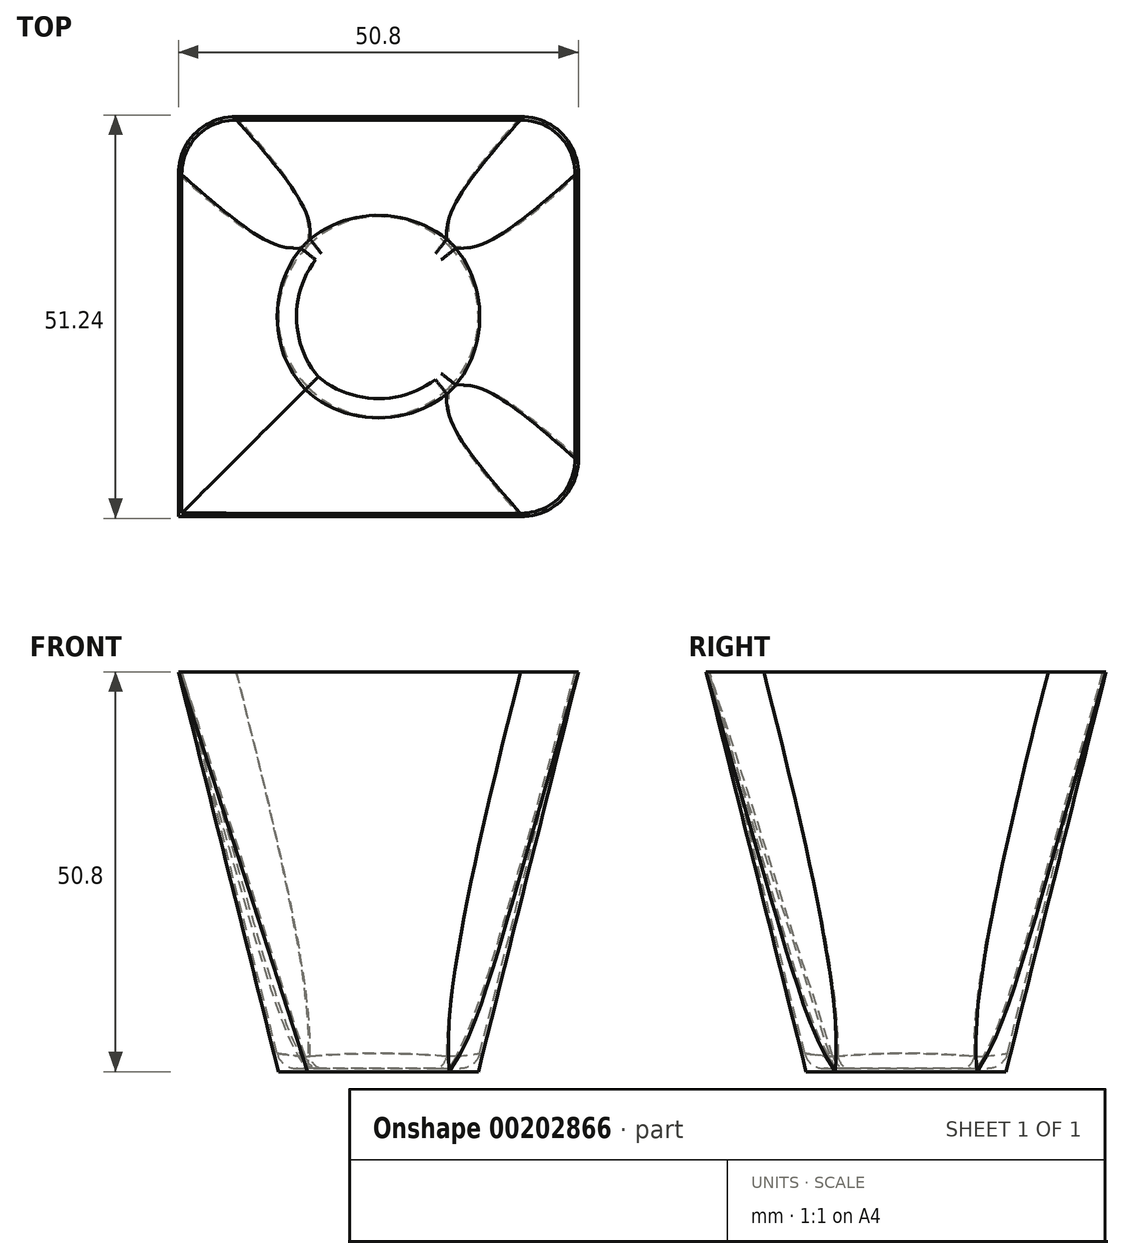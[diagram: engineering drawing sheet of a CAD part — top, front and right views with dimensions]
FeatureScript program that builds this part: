
annotation { "Feature Type Name" : "Feature", "Feature Type Description" : "" }
export const myFeature = defineFeature(function(context is Context, id is Id, definition is map)
    precondition{}
    {
        {
            var Q0;
            Q0=qCreatedBy(makeId("Top.planeOp"),FACE);
            var sketch = newSketch(context, id + "F0", { "sketchPlane" : qUnion([Q0])});
            skCircle(sketch, "E0", {"center": v(0, 0) * mm, "radius": 12.7 * mm});
            skSolve(sketch);
        }
        {
            var Q0;
            Q0=qCreatedBy(makeId("Top.planeOp"),FACE);
            cPlane(context, id + "F1", {"entities" : qUnion([Q0]), "cplaneType" : CPlaneType.OFFSET, "offset" : 50.8 * mm, "width" : 152.4 * mm, "height" : 152.4 * mm});
        }
        {
            var Q0;
            Q0=qCreatedBy(id+"F1.planeOp",FACE);
            var sketch = newSketch(context, id + "F2", { "sketchPlane" : qUnion([Q0])});
            skLineSegment(sketch, "E1.bottom", {"start": v(-25.4, 25.4) * mm, "end": v(25.4, 25.4) * mm});
            skLineSegment(sketch, "E1.top", {"start": v(-25.4, -25.4) * mm, "end": v(25.4, -25.4) * mm});
            skLineSegment(sketch, "E1.left", {"start": v(-25.4, 25.4) * mm, "end": v(-25.4, -25.4) * mm});
            skLineSegment(sketch, "E1.right", {"start": v(25.4, 25.4) * mm, "end": v(25.4, -25.4) * mm});
            skPoint(sketch, "E1.middle", {"position": v(0, 0) * mm});
            skSolve(sketch);
        }
        {
            var Q0;
            Q0=makeQuery(id+"F0.imprint","IMPRINT",FACE,{"disambiguationData":[TD([[makeQuery(id+"F0.imprint","IMPRINT",EDGE,{"derivedFrom":sQuery(id+"F0.wireOp",EDGE,"E0")}),1.0]])]});
            var Q1;
            Q1=makeQuery(id+"F2.imprint","IMPRINT",FACE,{"disambiguationData":[TD([[makeQuery(id+"F2.imprint","IMPRINT",EDGE,{"derivedFrom":sQuery(id+"F2.wireOp",EDGE,"E1.bottom")}),-1.0]])]});
            loft(context, id + "F3", {"sheetProfilesArray" : [{ "sheetProfileEntities" : qUnion([Q0]) }, { "sheetProfileEntities" : qUnion([Q1]) }]});
        }
        {
            var Q0;
            Q0=makeQuery(id+"F3.opLoft","SWEPT_EDGE",EDGE,{"disambiguationData":[OSD([sQuery(id+"F0.wireOp",EDGE,"E0"),sQuery(id+"F2.wireOp",EDGE,"E1.bottom"),sQuery(id+"F2.wireOp",EDGE,"E1.top"),sQuery(id+"F2.wireOp",EDGE,"E1.right")])]});
            var Q1;
            Q1=makeQuery(id+"F3.opLoft","SWEPT_EDGE",EDGE,{"disambiguationData":[OSD([sQuery(id+"F2.wireOp",EDGE,"E1.bottom"),sQuery(id+"F2.wireOp",EDGE,"E1.left")])]});
            var Q2;
            Q2=makeQuery(id+"F3.opLoft","SWEPT_EDGE",EDGE,{"disambiguationData":[OSD([sQuery(id+"F0.wireOp",EDGE,"E0"),sQuery(id+"F2.wireOp",EDGE,"E1.bottom"),sQuery(id+"F2.wireOp",EDGE,"E1.top"),sQuery(id+"F2.wireOp",EDGE,"E1.left")])]});
            var Q3;
            Q3=makeQuery(id+"F3.opLoft","SWEPT_EDGE",EDGE,{"disambiguationData":[OSD([sQuery(id+"F0.wireOp",EDGE,"E0"),sQuery(id+"F2.wireOp",EDGE,"E1.top"),sQuery(id+"F2.wireOp",EDGE,"E1.left"),sQuery(id+"F2.wireOp",EDGE,"E1.right")])]});
            fillet(context, id + "F4", {"entities" : qUnion([Q0, Q1, Q2, Q3]), "radius" : 7.62 * mm, "tangentPropagation" : true, "allowEdgeOverflow" : false});
        }
        {
            var Q0;
            Q0=makeQuery(id+"F3.opLoft","CAP_FACE",FACE,{"disambiguationData":[OSD([makeQuery(id+"F2.imprint","IMPRINT",FACE,{"disambiguationData":[TD([[makeQuery(id+"F2.imprint","IMPRINT",EDGE,{"derivedFrom":sQuery(id+"F2.wireOp",EDGE,"E1.bottom")}),-1.0]])]})])],"isStart":true});
            shell(context, id + "F5", {"entities" : qUnion([Q0]), "thickness" : .4 * mm});
        }
        {
            var Q0;
            Q0=makeQuery(id+"F5.opShell","OFFSET_FACE",FACE,{"disambiguationData":[OSD([makeQuery(id+"F0.imprint","IMPRINT",FACE,{"disambiguationData":[TD([[makeQuery(id+"F0.imprint","IMPRINT",EDGE,{"derivedFrom":sQuery(id+"F0.wireOp",EDGE,"E0")}),1.0]])]})])]});
            fillet(context, id + "F6", {"entities" : qUnion([Q0]), "radius" : 2.54 * mm, "tangentPropagation" : true, "allowEdgeOverflow" : false});
        }
    });
